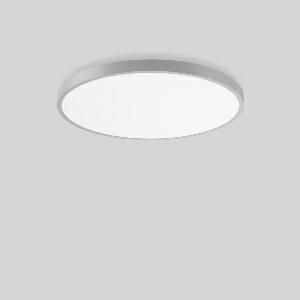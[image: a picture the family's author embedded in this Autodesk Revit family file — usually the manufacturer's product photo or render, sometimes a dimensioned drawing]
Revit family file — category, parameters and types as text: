
# Revit family: triona_round_a_312387_004_1_730_9aee
name_source: partatom
category: Lighting Fixtures
units: mm (PartAtom-declared; Revit-internal decimal feet)

## family parameters
Cut with Voids When Loaded = No
Host = Face
Light Source = No
Part Type = Normal
Room Calculation Point = No
Round Connector Dimension = Use Diameter
Shared = No

## types (1)
- TRIONA round A (1 x LED Modul 840, 8300 lm, 4000)
    Apparent Load = 80 VA
    CIE Flux Codes = 49 80 96 100 100
    Color Rendering = 80
    Color Temperature = 4000
    Default Elevation = 1800 mm
    Description = Series: TRIONA round
Decorative round LED surface-mounted luminaire. Flat, seamless frame: aluminium extrusion profile, powder coated. Cover made of sheet steel, powder-coated. Light emission through a diffuser: plastic, opal. Lightguide and diffuser made of non-yellowing plastic (PMMA). Lateral light emission (RZB SIDELITE technology) for above-average homogeneous light distribution. Suitable for Ceiling mounting, Wall (surface). Tool-free mounting via bayonet connection. Electronic ballast included. Very easy installation thanks to Plug+Play connection. With Casambi smart+free Bluetooth control for wireless network and operation using Android / iOS devices, free app available for download. 
Colour: silver, matt (approx. RAL 9006)
Diameter: 845 mm
Height: 88 mm
Lamp: LED
Socket: without socket
Colour temperature: 4000K
Colour rendering index (CRI): 80
System power: 80 W
Rated luminous flux: 8300 lm
Luminous efficiency: 104 lm/W
Control gear: Dimmable Bluetooth converter
Protection class: I
Type of protection: IP 20
    Height = 88 mm
    Lamp = 1 x LED Modul 840
    Lamp Light Flux = 8300 lm
    Lamp count = 1
    Length = 845 mm
    Lifetime = 50000 h
    Luminous efficacy = 104 lm/W
    Manufacturer = RZB
    ModVariant = No
    Model = 312387.004.1.730
    Mounting Place = Ceiling
    Mounting Type = Surface mounted
    Number of Poles = 1
    OnlyDefault = Yes
    Power Factor = 1
    Product Name = TRIONA round A
    Product group = Surface mounted modular luminaires
    ProductGroupID = 306
    Protection Class = Protection class I
    Protection Degree = IP 20
    RLX_Detail_Level = 1
    RLX_Emergency_Light_Flux = 0 lm
    RLX_Emergency_Type = 0
    RLX_Emergency_Type_DB = No
    RlxData = <blob elided: 34449 chars, md5=1d0a0fdc>
    Socket = socket
    Standby Power = 0 W
    System Light Flux = 8300 lm
    System Power = 80 W
    Type Comments = Product without accessories
    Type Image = 312388.004.jpg
    URL = http://relux.com
    VarID = ---
    Voltage = 230 V
    Voltage Range = 220-240 V
    Weight = 0.00 kg
    Width = 0 mm  [stored 0 ft]

note: [stored X ft] marks values corroborated as IEEE doubles in the binary element streams (Revit-internal decimal feet)

## geometry (parser evidence)
native form markers: Blend x4, Sweep x9
no freeform markers — native parametric forms only
